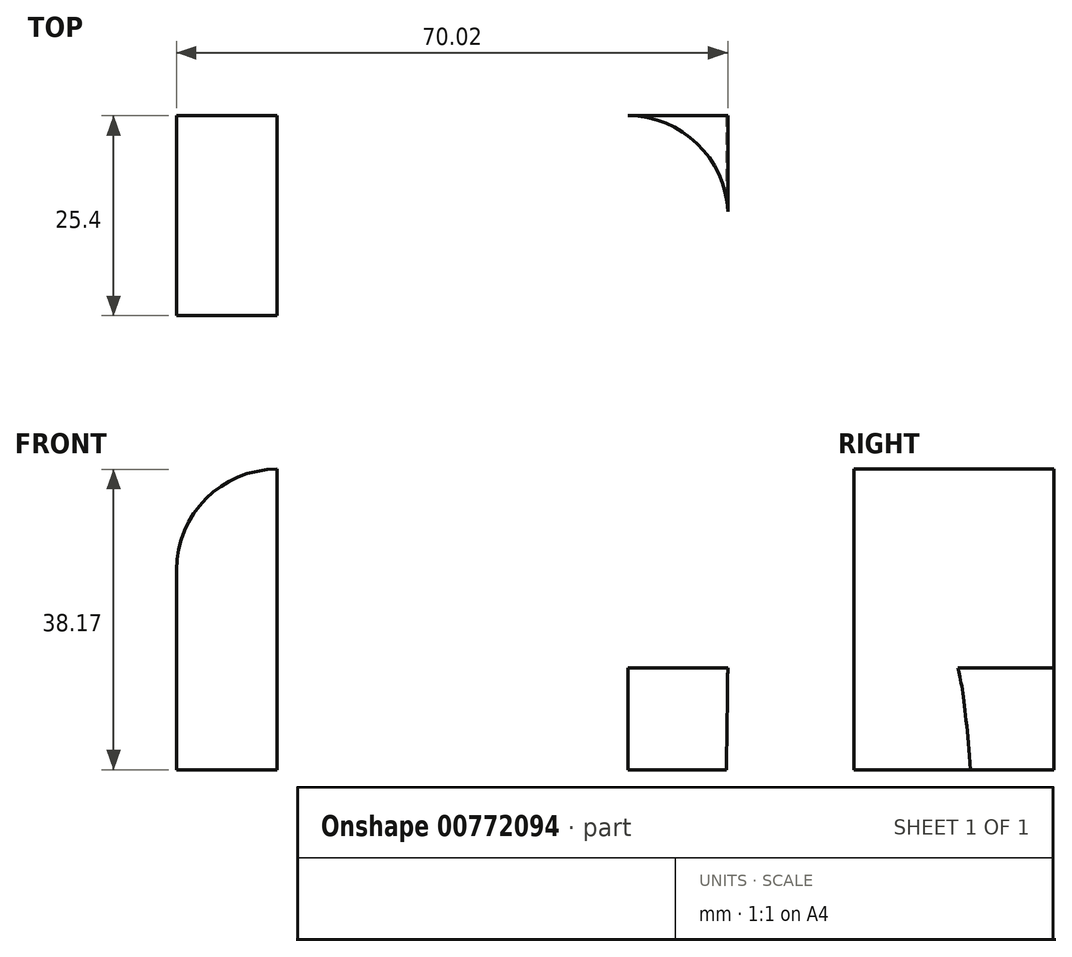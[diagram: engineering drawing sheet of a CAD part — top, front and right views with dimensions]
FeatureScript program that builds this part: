
annotation { "Feature Type Name" : "Feature", "Feature Type Description" : "" }
export const myFeature = defineFeature(function(context is Context, id is Id, definition is map)
    precondition{}
    {
        {
            var Q0;
            Q0=qCreatedBy(makeId("Front.planeOp"),FACE);
            var sketch = newSketch(context, id + "F0", { "sketchPlane" : qUnion([Q0])});
            skLineSegment(sketch, "E0", {"start": v(0, 0) * mm, "end": v(69.85, 0) * mm});
            skLineSegment(sketch, "E1", {"start": v(0, 0) * mm, "end": v(0, 38.2) * mm});
            skLineSegment(sketch, "E2", {"start": v(0, 38.2) * mm, "end": v(25.57, 38.2) * mm});
            skLineSegment(sketch, "E3", {"start": v(25.57, 38.2) * mm, "end": v(25.57, 12.9) * mm});
            skLineSegment(sketch, "E4", {"start": v(25.57, 12.9) * mm, "end": v(70.02, 12.9) * mm});
            skLineSegment(sketch, "E5", {"start": v(69.85, 0) * mm, "end": v(70.02, 12.9) * mm});
            skSolve(sketch);
        }
        {
            var Q0;
            Q0 = qSketchRegion(id + "F0", true);
            extrude(context, id + "F1", {"entities" : qUnion([Q0]), "depth" : 25.4 * mm, "offsetDistance" : 25.4 * mm});
        }
        {
            var Q0;
            Q0=makeQuery(id+"F1.opExtrude","SWEPT_FACE",FACE,{"disambiguationData":[OSD([sQuery(id+"F0.wireOp",EDGE,"E4")])]});
            var sketch = newSketch(context, id + "F2", { "sketchPlane" : qUnion([Q0])});
            skLineSegment(sketch, "E6", {"start": v(25.57, 0) * mm, "end": v(31.88, 0) * mm});
            skLineSegment(sketch, "E7", {"start": v(25.57, -12.7) * mm, "end": v(70.02, -12.7) * mm});
            skLineSegment(sketch, "E8", {"start": v(31.88, -12.7) * mm, "end": v(36.23, -12.7) * mm});
            skLineSegment(sketch, "E9", {"start": v(38.27, 0) * mm, "end": v(38.27, -25.4) * mm});
            skLineSegment(sketch, "E10", {"start": v(57.32, 0) * mm, "end": v(57.32, -25.4) * mm});
            skCircle(sketch, "E11", {"center": v(38.27, -12.7) * mm, "radius": 6.35 * mm});
            skCircle(sketch, "E12", {"center": v(57.32, -12.7) * mm, "radius": 6.35 * mm});
            skLineSegment(sketch, "E13", {"start": v(38.27, -6.35) * mm, "end": v(57.32, -6.35) * mm});
            skLineSegment(sketch, "E14", {"start": v(38.27, -19.05) * mm, "end": v(57.32, -19.05) * mm});
            skLineSegment(sketch, "E15", {"start": v(70.02, -12.7) * mm, "end": v(83.12, -12.7) * mm});
            skArc(sketch, "E16", {"start": v(57.32, -25.4) * mm, "mid": v(70.03, -12.7) * mm, "end": v(57.32, 0) * mm});
            skSolve(sketch);
        }
        {
            var Q0;
            {var subQ0=sQuery(id+"F2.wireOp",EDGE,"E8");var subQ1=sQuery(id+"F2.wireOp",EDGE,"E7");var subQ2=makeQuery(id+"F2.imprint","INTERSECT",VERTEX,{"disambiguationData":[OD(1.0)],"derivedFrom":[subQ1,subQ0]});Q0=makeQuery(id+"F2.imprint","IMPRINT",FACE,{"disambiguationData":[TD([[makeQuery(id+"F2.imprint","IMPRINT",EDGE,{"disambiguationData":[TD([[subQ2,-1.0]])],"derivedFrom":subQ1}),1.0]])]});}
            var Q1;
            {var subQ0=sQuery(id+"F2.wireOp",EDGE,"E8");var subQ1=sQuery(id+"F2.wireOp",EDGE,"E7");var subQ2=makeQuery(id+"F2.imprint","INTERSECT",VERTEX,{"disambiguationData":[OD(1.0)],"derivedFrom":[subQ1,subQ0]});Q1=makeQuery(id+"F2.imprint","IMPRINT",FACE,{"disambiguationData":[TD([[makeQuery(id+"F2.imprint","IMPRINT",EDGE,{"disambiguationData":[TD([[subQ2,-1.0]])],"derivedFrom":subQ1}),-1.0]])]});}
            var Q2;
            {var subQ0=sQuery(id+"F2.wireOp",EDGE,"E9");var subQ1=sQuery(id+"F2.wireOp",EDGE,"E7");var subQ2=makeQuery(id+"F2.imprint","INTERSECT",VERTEX,{"derivedFrom":[subQ1,subQ0]});Q2=makeQuery(id+"F2.imprint","IMPRINT",FACE,{"disambiguationData":[TD([[makeQuery(id+"F2.imprint","IMPRINT",EDGE,{"disambiguationData":[TD([[subQ2,-1.0]])],"derivedFrom":subQ1}),1.0]])]});}
            var Q3;
            {var subQ0=sQuery(id+"F2.wireOp",EDGE,"E9");var subQ1=sQuery(id+"F2.wireOp",EDGE,"E7");var subQ2=makeQuery(id+"F2.imprint","INTERSECT",VERTEX,{"derivedFrom":[subQ1,subQ0]});Q3=makeQuery(id+"F2.imprint","IMPRINT",FACE,{"disambiguationData":[TD([[makeQuery(id+"F2.imprint","IMPRINT",EDGE,{"disambiguationData":[TD([[subQ2,-1.0]])],"derivedFrom":subQ1}),-1.0]])]});}
            var Q4;
            {var subQ0=sQuery(id+"F2.wireOp",EDGE,"E12");var subQ1=sQuery(id+"F2.wireOp",EDGE,"E7");var subQ2=makeQuery(id+"F2.imprint","INTERSECT",VERTEX,{"disambiguationData":[OD(0.0)],"derivedFrom":[subQ1,subQ0]});Q4=makeQuery(id+"F2.imprint","IMPRINT",FACE,{"disambiguationData":[TD([[makeQuery(id+"F2.imprint","IMPRINT",EDGE,{"disambiguationData":[TD([[subQ2,-1.0]])],"derivedFrom":subQ1}),1.0]])]});}
            var Q5;
            {var subQ0=sQuery(id+"F2.wireOp",EDGE,"E12");var subQ1=sQuery(id+"F2.wireOp",EDGE,"E7");var subQ2=makeQuery(id+"F2.imprint","INTERSECT",VERTEX,{"disambiguationData":[OD(0.0)],"derivedFrom":[subQ1,subQ0]});Q5=makeQuery(id+"F2.imprint","IMPRINT",FACE,{"disambiguationData":[TD([[makeQuery(id+"F2.imprint","IMPRINT",EDGE,{"disambiguationData":[TD([[subQ2,-1.0]])],"derivedFrom":subQ1}),-1.0]])]});}
            var Q6;
            {var subQ0=sQuery(id+"F2.wireOp",EDGE,"E10");var subQ1=sQuery(id+"F2.wireOp",EDGE,"E7");var subQ2=makeQuery(id+"F2.imprint","INTERSECT",VERTEX,{"derivedFrom":[subQ1,subQ0]});Q6=makeQuery(id+"F2.imprint","IMPRINT",FACE,{"disambiguationData":[TD([[makeQuery(id+"F2.imprint","IMPRINT",EDGE,{"disambiguationData":[TD([[subQ2,-1.0]])],"derivedFrom":subQ1}),1.0]])]});}
            var Q7;
            {var subQ0=sQuery(id+"F2.wireOp",EDGE,"E10");var subQ1=sQuery(id+"F2.wireOp",EDGE,"E7");var subQ2=makeQuery(id+"F2.imprint","INTERSECT",VERTEX,{"derivedFrom":[subQ1,subQ0]});Q7=makeQuery(id+"F2.imprint","IMPRINT",FACE,{"disambiguationData":[TD([[makeQuery(id+"F2.imprint","IMPRINT",EDGE,{"disambiguationData":[TD([[subQ2,-1.0]])],"derivedFrom":subQ1}),-1.0]])]});}
            var Q8;
            {var subQ5=sQuery(id+"F2.wireOp",EDGE,"E13");Q8=makeQuery(id+"F2.imprint","IMPRINT",FACE,{"disambiguationData":[TD([[makeQuery(id+"F2.imprint","IMPRINT",EDGE,{"derivedFrom":subQ5}),-1.0]])]});}
            var Q9;
            {var subQ5=sQuery(id+"F2.wireOp",EDGE,"E14");Q9=makeQuery(id+"F2.imprint","IMPRINT",FACE,{"disambiguationData":[TD([[makeQuery(id+"F2.imprint","IMPRINT",EDGE,{"derivedFrom":subQ5}),1.0]])]});}
            var Q10;
            {var subQ0=sQuery(id+"F2.wireOp",EDGE,"E15");var subQ3=sQuery(id+"F2.wireOp",EDGE,"E16");var subQ4=makeQuery(id+"F2.imprint","INTERSECT",VERTEX,{"derivedFrom":[subQ0,subQ3]});Q10=makeQuery(id+"F2.imprint","IMPRINT",FACE,{"disambiguationData":[TD([[makeQuery(id+"F2.imprint","IMPRINT",EDGE,{"disambiguationData":[TD([[subQ4,1.0]])],"derivedFrom":subQ3}),1.0]])]});}
            var Q11;
            {var subQ0=sQuery(id+"F2.wireOp",EDGE,"E16");var subQ1=sQuery(id+"F0.wireOp",EDGE,"E4");var subQ4=makeQuery(id+"F1.opExtrude","SWEPT_EDGE",EDGE,{"disambiguationData":[OSD([subQ1,sQuery(id+"F0.wireOp",EDGE,"E5")])]});var subQ5=makeQuery(id+"F2.imprint","INTERSECT",VERTEX,{"disambiguationData":[OD(1.0)],"derivedFrom":[subQ4,subQ0]});Q11=makeQuery(id+"F2.imprint","IMPRINT",FACE,{"disambiguationData":[TD([[makeQuery(id+"F2.imprint","IMPRINT",EDGE,{"disambiguationData":[TD([[subQ5,-1.0]])],"derivedFrom":subQ0}),-1.0]])]});}
            var Q12;
            {var subQ0=sQuery(id+"F2.wireOp",EDGE,"E16");var subQ1=sQuery(id+"F0.wireOp",EDGE,"E4");var subQ2=makeQuery(id+"F1.opExtrude","CAP_EDGE",EDGE,{"disambiguationData":[OSD([subQ1])],"isStart":false});var subQ3=makeQuery(id+"F2.imprint","INTERSECT",VERTEX,{"derivedFrom":[subQ2,subQ0]});Q12=makeQuery(id+"F2.imprint","IMPRINT",FACE,{"disambiguationData":[TD([[makeQuery(id+"F2.imprint","IMPRINT",EDGE,{"disambiguationData":[TD([[subQ3,-1.0]])],"derivedFrom":subQ0}),-1.0]])]});}
            extrude(context, id + "F3", {"entities" : qUnion([Q0, Q1, Q2, Q3, Q4, Q5, Q6, Q7, Q8, Q9, Q10, Q11, Q12]), "operationType" : NewBodyOperationType.REMOVE, "endBound" : BoundingType.THROUGH_ALL, "oppositeDirection" : true, "depth" : 25.4 * mm, "offsetDistance" : 25.4 * mm});
        }
        {
            var Q0;
            Q0=makeQuery(id+"F1.opExtrude","CAP_FACE",FACE,{"disambiguationData":[OSD([sQuery(id+"F0.wireOp",EDGE,"E0"),sQuery(id+"F0.wireOp",EDGE,"E1"),sQuery(id+"F0.wireOp",EDGE,"E2"),sQuery(id+"F0.wireOp",EDGE,"E3"),sQuery(id+"F0.wireOp",EDGE,"E4"),sQuery(id+"F0.wireOp",EDGE,"E5")])],"isStart":false});
            var sketch = newSketch(context, id + "F4", { "sketchPlane" : qUnion([Q0])});
            skLineSegment(sketch, "E17", {"start": v(0, 38.2) * mm, "end": v(0, 25.39) * mm});
            skLineSegment(sketch, "E18", {"start": v(0, 25.39) * mm, "end": v(25.57, 25.39) * mm});
            skLineSegment(sketch, "E19", {"start": v(12.79, 38.2) * mm, "end": v(12.79, 0) * mm});
            skPoint(sketch, "E19.endSnap0", {"position": v(12.79, 25.39) * mm});
            skCircle(sketch, "E20", {"center": v(12.79, 25.39) * mm, "radius": 6.35 * mm});
            skArc(sketch, "E21", {"start": v(25.57, 25.39) * mm, "mid": v(12.79, 38.17) * mm, "end": v(0, 25.39) * mm});
            skSolve(sketch);
        }
        {
            var Q0;
            {var subQ0=sQuery(id+"F4.wireOp",EDGE,"E19");var subQ1=sQuery(id+"F4.wireOp",EDGE,"E18");var subQ2=makeQuery(id+"F4.imprint","INTERSECT",VERTEX,{"derivedFrom":[subQ1,subQ0]});Q0=makeQuery(id+"F4.imprint","IMPRINT",FACE,{"disambiguationData":[TD([[makeQuery(id+"F4.imprint","IMPRINT",EDGE,{"disambiguationData":[TD([[subQ2,-1.0]])],"derivedFrom":subQ1}),-1.0]])]});}
            var Q1;
            {var subQ0=sQuery(id+"F4.wireOp",EDGE,"E17");Q1=makeQuery(id+"F4.imprint","IMPRINT",FACE,{"disambiguationData":[TD([[makeQuery(id+"F4.imprint","IMPRINT",EDGE,{"derivedFrom":subQ0}),-1.0]])]});}
            var Q2;
            {var subQ0=sQuery(id+"F4.wireOp",EDGE,"E19");var subQ1=makeQuery(id+"F1.opExtrude","CAP_EDGE",EDGE,{"disambiguationData":[OSD([sQuery(id+"F0.wireOp",EDGE,"E2")])],"isStart":false});var subQ2=makeQuery(id+"F4.imprint","INTERSECT",VERTEX,{"derivedFrom":[subQ1,subQ0]});Q2=makeQuery(id+"F4.imprint","IMPRINT",FACE,{"disambiguationData":[TD([[makeQuery(id+"F4.imprint","IMPRINT",EDGE,{"disambiguationData":[TD([[subQ2,-1.0]])],"derivedFrom":subQ0}),1.0]])]});}
            var Q3;
            {var subQ0=sQuery(id+"F4.wireOp",EDGE,"E19");var subQ1=sQuery(id+"F4.wireOp",EDGE,"E18");var subQ2=makeQuery(id+"F4.imprint","INTERSECT",VERTEX,{"derivedFrom":[subQ1,subQ0]});Q3=makeQuery(id+"F4.imprint","IMPRINT",FACE,{"disambiguationData":[TD([[makeQuery(id+"F4.imprint","IMPRINT",EDGE,{"disambiguationData":[TD([[subQ2,-1.0]])],"derivedFrom":subQ1}),1.0]])]});}
            var Q4;
            {var subQ0=sQuery(id+"F4.wireOp",EDGE,"E20");var subQ1=sQuery(id+"F4.wireOp",EDGE,"E18");var subQ2=makeQuery(id+"F4.imprint","INTERSECT",VERTEX,{"disambiguationData":[OD(0.0)],"derivedFrom":[subQ1,subQ0]});Q4=makeQuery(id+"F4.imprint","IMPRINT",FACE,{"disambiguationData":[TD([[makeQuery(id+"F4.imprint","IMPRINT",EDGE,{"disambiguationData":[TD([[subQ2,-1.0]])],"derivedFrom":subQ1}),1.0]])]});}
            var Q5;
            {var subQ0=sQuery(id+"F4.wireOp",EDGE,"E20");var subQ1=sQuery(id+"F4.wireOp",EDGE,"E18");var subQ2=makeQuery(id+"F4.imprint","INTERSECT",VERTEX,{"disambiguationData":[OD(0.0)],"derivedFrom":[subQ1,subQ0]});Q5=makeQuery(id+"F4.imprint","IMPRINT",FACE,{"disambiguationData":[TD([[makeQuery(id+"F4.imprint","IMPRINT",EDGE,{"disambiguationData":[TD([[subQ2,-1.0]])],"derivedFrom":subQ1}),-1.0]])]});}
            extrude(context, id + "F5", {"entities" : qUnion([Q0, Q1, Q2, Q3, Q4, Q5]), "operationType" : NewBodyOperationType.REMOVE, "oppositeDirection" : true, "depth" : 25.4 * mm, "offsetDistance" : 25.4 * mm});
        }
    });
